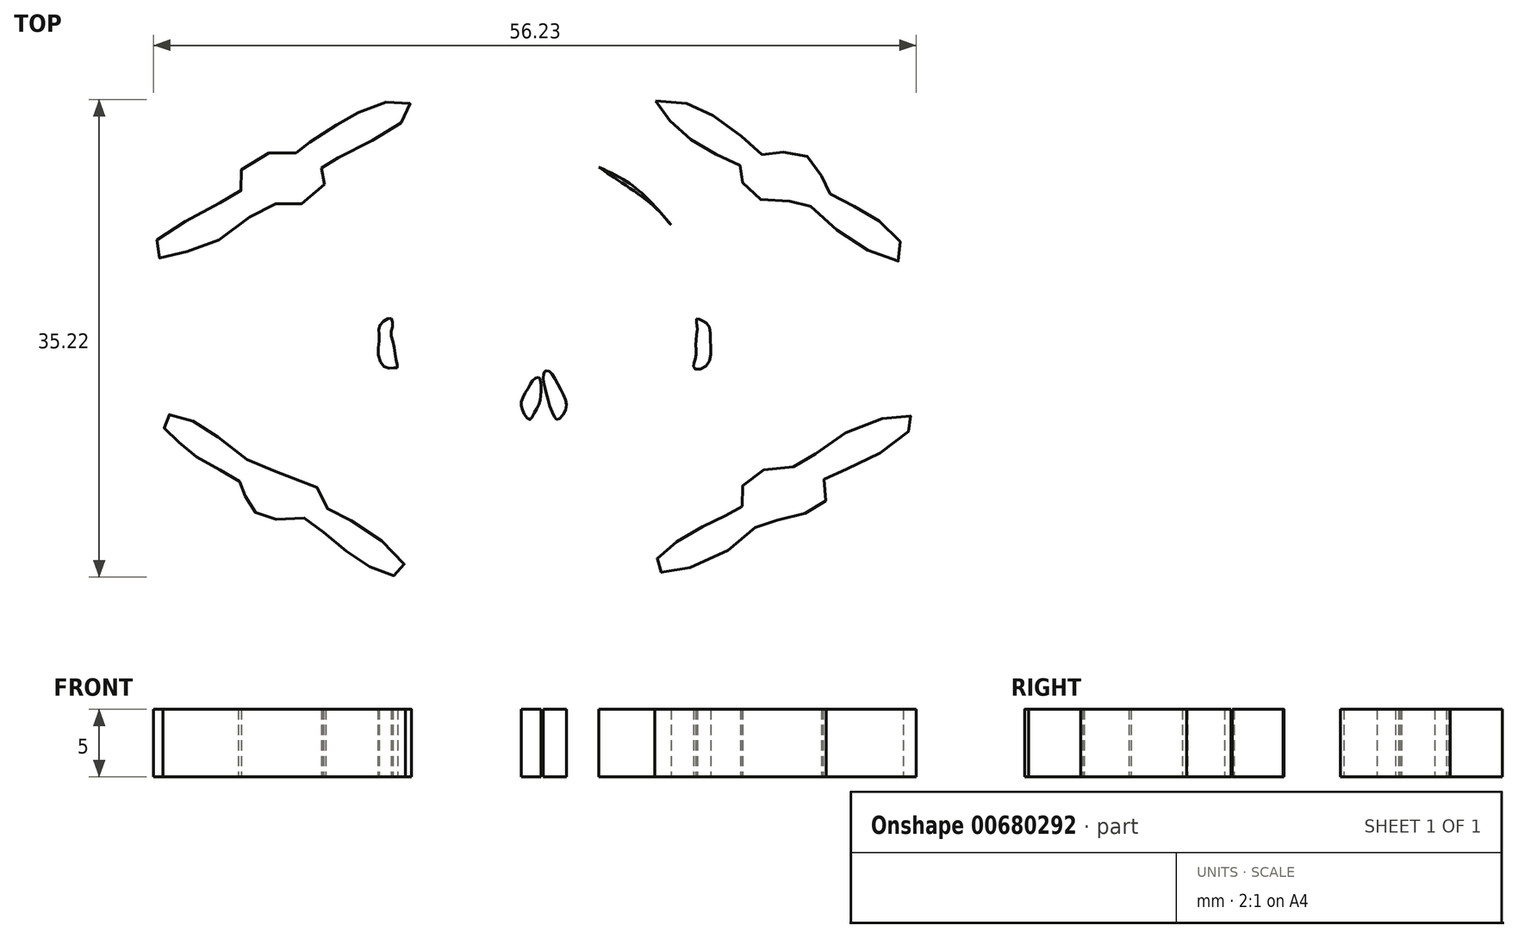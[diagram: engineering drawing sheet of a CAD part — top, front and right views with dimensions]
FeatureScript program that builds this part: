
annotation { "Feature Type Name" : "Feature", "Feature Type Description" : "" }
export const myFeature = defineFeature(function(context is Context, id is Id, definition is map)
    precondition{}
    {
        {
            var Q0;
            Q0=qCreatedBy(makeId("Top.planeOp"),FACE);
            var sketch = newSketch(context, id + "F0", { "sketchPlane" : qUnion([Q0])});
            skFitSpline(sketch, "E0", {"points": [v(10.13, 8.26) * mm, v(10.2, 8.23) * mm, v(10.31, 8.24) * mm, v(10.54, 8.33) * mm, v(11.27, 8.71) * mm, v(11.62, 8.94) * mm, v(11.74, 9.02) * mm, v(11.88, 9.1) * mm, v(12.05, 9.17) * mm, v(12.17, 9.2) * mm, v(12.52, 9.37) * mm, v(13, 9.64) * mm, v(13.46, 9.93) * mm, v(13.75, 10.16) * mm, v(13.84, 10.24) * mm, v(13.9, 10.28) * mm, v(14, 10.28) * mm, v(14.12, 10.26) * mm, v(14.35, 10.23) * mm, v(14.46, 10.12) * mm, v(14.7, 9.87) * mm, v(15.04, 9.58) * mm, v(15.42, 9.37) * mm, v(15.73, 9.26) * mm, v(15.89, 9.21) * mm, v(15.92, 9.01) * mm, v(15.8, 8.92) * mm, v(15.64, 8.77) * mm, v(15.34, 8.59) * mm, v(14.9, 8.31) * mm, v(14.46, 8.04) * mm, v(14.12, 7.8) * mm, v(13.92, 7.64) * mm, v(13.79, 7.51) * mm, v(13.68, 7.48) * mm, v(13.63, 7.45) * mm, v(13.56, 7.42) * mm, v(13.46, 7.34) * mm, v(13.22, 7.14) * mm, v(13.07, 7) * mm, v(12.88, 6.86) * mm, v(12.7, 6.72) * mm, v(12.57, 6.6) * mm, v(12.32, 6.44) * mm, v(12.11, 6.26) * mm, v(11.93, 6.12) * mm, v(11.5, 5.75) * mm, v(11.53, 5.38) * mm, v(11.56, 5.18) * mm, v(11.6, 4.96) * mm, v(11.63, 4.7) * mm, v(11.69, 4.2) * mm, v(11.72, 3.46) * mm, v(11.73, 2.53) * mm, v(11.73, 1.6) * mm, v(11.69, 0.57) * mm, v(11.55, -1.09) * mm, v(11.55, -1.68) * mm, v(11.39, -2.1) * mm, v(11.08, -2.47) * mm, v(10.9, -3.07) * mm, v(10.48, -3.5) * mm, v(10.24, -3.8) * mm, v(10.04, -3.97) * mm, v(10.22, -4.19) * mm, v(10.47, -4.68) * mm, v(11.06, -5.12) * mm, v(11.54, -5.58) * mm, v(12.28, -6.13) * mm, v(13.05, -6.75) * mm, v(13.79, -7.3) * mm, v(14.5, -7.7) * mm, v(15.17, -8.35) * mm, v(15.89, -8.8) * mm, v(15.89, -9.05) * mm, v(15.6, -9.3) * mm, v(15.18, -9.48) * mm, v(14.73, -9.82) * mm, v(14.3, -10.16) * mm, v(13.5, -9.79) * mm, v(12.57, -9.13) * mm, v(11.8, -8.7) * mm, v(10.62, -8.09) * mm, v(10.04, -7.78) * mm, v(9.78, -7.87) * mm, v(9.5, -7.97) * mm, v(9.18, -8.2) * mm, v(8.58, -8.01) * mm, v(8.18, -7.82) * mm, v(7.86, -8) * mm, v(7.23, -8.25) * mm, v(6.68, -8.32) * mm, v(6.3, -8.03) * mm, v(6.17, -7.6) * mm, v(6.4, -6.99) * mm, v(6.6, -6.88) * mm, v(6.02, -6.38) * mm, v(5.65, -6.15) * mm, v(5.28, -5.98) * mm, v(4.82, -5.8) * mm, v(4.78, -6) * mm, v(4.83, -6.32) * mm, v(4.76, -6.63) * mm, v(4.7, -6.86) * mm, v(4.66, -7) * mm, v(4.73, -7.22) * mm, v(4.78, -7.55) * mm, v(4.72, -8.25) * mm, v(4.56, -8.76) * mm, v(4.54, -9.09) * mm, v(4.35, -9.45) * mm, v(4.22, -9.72) * mm, v(4.2, -9.9) * mm, v(3.75, -9.98) * mm, v(3.47, -10) * mm, v(2.92, -10.02) * mm, v(1.78, -10.18) * mm, v(0.94, -10.13) * mm, v(0.27, -10.2) * mm, v(-0.56, -10.11) * mm, v(-1.03, -10.13) * mm, v(-1.83, -9.96) * mm, v(-2.57, -9.93) * mm, v(-3.05, -9.77) * mm, v(-3.28, -9.77) * mm, v(-3.46, -9) * mm, v(-3.75, -8.08) * mm, v(-3.96, -6.87) * mm, v(-3.96, -6.34) * mm, v(-4.25, -6.17) * mm, v(-4.65, -6.04) * mm, v(-5.1, -5.85) * mm, v(-5.39, -5.9) * mm, v(-5.76, -5.98) * mm, v(-5.9, -6.24) * mm, v(-5.86, -6.56) * mm, v(-5.88, -7.03) * mm, v(-5.83, -7.42) * mm, v(-5.87, -7.7) * mm, v(-6.03, -7.86) * mm, v(-6.24, -7.99) * mm, v(-6.65, -8.04) * mm, v(-7.07, -7.88) * mm, v(-7.25, -7.8) * mm, v(-7.7, -7.52) * mm, v(-7.92, -7.27) * mm, v(-8.28, -7.06) * mm, v(-8.54, -7.21) * mm, v(-8.92, -7.31) * mm, v(-9.32, -7.53) * mm, v(-9.97, -7.8) * mm, v(-10.9, -8.41) * mm, v(-11.44, -8.59) * mm, v(-12.43, -9.17) * mm, v(-13.25, -9.75) * mm, v(-14.01, -10.02) * mm, v(-14.3, -10.13) * mm, v(-15.13, -9.67) * mm, v(-15.87, -9.15) * mm, v(-15.93, -8.83) * mm, v(-14.98, -8.3) * mm, v(-14.01, -7.45) * mm, v(-12.66, -6.53) * mm, v(-11.69, -5.72) * mm, v(-10.5, -4.66) * mm, v(-9.37, -3.7) * mm, v(-9, -3.24) * mm, v(-9.47, -2.58) * mm, v(-9.77, -1.84) * mm, v(-9.93, -1.1) * mm, v(-9.92, -0.44) * mm, v(-9.98, 1.9) * mm, v(-10.07, 3.11) * mm, v(-9.95, 4.02) * mm, v(-10.51, 4.66) * mm, v(-11.44, 5.26) * mm, v(-12.28, 6.1) * mm, v(-13.46, 6.98) * mm, v(-15.55, 8.33) * mm, v(-16.03, 8.77) * mm, v(-16.33, 9.04) * mm, v(-15.84, 9.29) * mm, v(-15.1, 9.58) * mm, v(-14.7, 10.05) * mm, v(-14.38, 10.23) * mm, v(-13.96, 9.9) * mm, v(-13.19, 9.6) * mm, v(-12.35, 9.07) * mm, v(-11.41, 8.64) * mm, v(-10.76, 8.11) * mm, v(-9.84, 7.8) * mm, v(-9.25, 7.4) * mm, v(-8.95, 7.46) * mm, v(-8.25, 8.48) * mm, v(-7.51, 9.34) * mm, v(-5.55, 11.08) * mm, v(-4.2, 11.8) * mm, v(-2.84, 12.46) * mm, v(-0.14, 13.03) * mm, v(3.77, 12.96) * mm, v(5.69, 11.91) * mm, v(8.93, 9.56) * mm, v(10.13, 8.26) * mm]});
            skLineSegment(sketch, "E1", {"start": v(10.13, 8.26) * mm, "end": v(10.13, 8.26) * mm});
            skFitSpline(sketch, "E2", {"points": [v(3.77, 12.96) * mm, v(6.66, 11.57) * mm, v(8.5, 10.09) * mm, v(10.13, 8.26) * mm], "startDerivative": vector(8.44, -3.6) * mm, "endDerivative": vector(5.03, -5.92) * mm});
            skFitSpline(sketch, "E3", {"points": [v(-17.54, 13.55) * mm, v(-17.12, 13.84) * mm, v(-16.27, 14.5) * mm, v(-14.26, 15.8) * mm, v(-13.06, 16.48) * mm, v(-11.37, 17.16) * mm, v(-9.48, 17.44) * mm, v(-9.03, 16.93) * mm, v(-9.76, 15.82) * mm, v(-12.03, 14.42) * mm, v(-14.8, 13.04) * mm, v(-15.57, 12.62) * mm, v(-15.63, 12.27) * mm, v(-15.33, 11.63) * mm, v(-16.24, 10.35) * mm, v(-18.03, 9.62) * mm, v(-19.43, 9.81) * mm, v(-21.63, 8.25) * mm, v(-24.27, 6.65) * mm, v(-26.6, 6.05) * mm, v(-27.81, 5.88) * mm, v(-27.94, 6.86) * mm, v(-26.11, 8.27) * mm, v(-23.05, 9.92) * mm, v(-21.6, 10.64) * mm, v(-21.74, 11.4) * mm, v(-21.35, 12.6) * mm, v(-18.98, 13.63) * mm, v(-17.54, 13.55) * mm]});
            skFitSpline(sketch, "E4", {"points": [v(-23.26, -7.4) * mm, v(-24.07, -6.87) * mm, v(-25.7, -5.93) * mm, v(-26.37, -5.8) * mm, v(-27.2, -5.77) * mm, v(-27.33, -6.13) * mm, v(-27.27, -6.68) * mm, v(-26.92, -7.07) * mm, v(-26.36, -7.57) * mm, v(-25.89, -8.06) * mm, v(-25.33, -8.5) * mm, v(-24.1, -9.38) * mm, v(-23.26, -9.76) * mm, v(-22.21, -10.4) * mm, v(-21.77, -10.67) * mm, v(-21.46, -10.72) * mm, v(-21.32, -11.33) * mm, v(-21.28, -11.76) * mm, v(-21.1, -12.4) * mm, v(-20.7, -12.86) * mm, v(-19.81, -13.25) * mm, v(-19.2, -13.42) * mm, v(-18.27, -13.46) * mm, v(-16.88, -13.36) * mm, v(-16, -13.99) * mm, v(-15.41, -14.5) * mm, v(-14.49, -15.34) * mm, v(-13, -16.34) * mm, v(-12.16, -16.92) * mm, v(-11.25, -17.3) * mm, v(-10.18, -17.65) * mm, v(-9.58, -17.63) * mm, v(-9.53, -16.8) * mm, v(-10.65, -15.48) * mm, v(-12.08, -14.43) * mm, v(-13.94, -13.26) * mm, v(-14.78, -12.9) * mm, v(-15.54, -12.35) * mm, v(-15.53, -11.69) * mm, v(-18.2, -9.88) * mm, v(-19.92, -10) * mm, v(-21.68, -8.52) * mm, v(-23.26, -7.4) * mm]});
            skFitSpline(sketch, "E5", {"points": [v(15.38, -12.52) * mm, v(14.94, -12.86) * mm, v(13.62, -13.41) * mm, v(12.15, -14.17) * mm, v(10.18, -15.35) * mm, v(9.1, -16.35) * mm, v(8.97, -17.01) * mm, v(9.68, -17.43) * mm, v(12.25, -16.72) * mm, v(15.7, -14.77) * mm, v(17.03, -13.49) * mm, v(18.85, -13.57) * mm, v(20.76, -12.53) * mm, v(21.55, -12) * mm, v(21.34, -10.7) * mm, v(21.84, -10.2) * mm, v(24.38, -9.21) * mm, v(27.11, -7.43) * mm, v(28.2, -6.1) * mm, v(27.2, -5.76) * mm, v(24.8, -6.35) * mm, v(21.26, -8.13) * mm, v(19.9, -9.42) * mm, v(17.86, -9.63) * mm, v(15.99, -10.33) * mm, v(15.24, -11.53) * mm, v(15.38, -12.52) * mm]});
            skFitSpline(sketch, "E6", {"points": [v(9, 17.4) * mm, v(9.65, 16.33) * mm, v(11.3, 14.77) * mm, v(12.95, 13.7) * mm, v(15.01, 12.77) * mm, v(15.38, 12.36) * mm, v(15.41, 11.33) * mm, v(16.45, 10.23) * mm, v(18.66, 9.96) * mm, v(19.83, 10) * mm, v(21.83, 8.32) * mm, v(24.71, 6.34) * mm, v(27, 5.63) * mm, v(27.18, 6.63) * mm, v(25.83, 8.28) * mm, v(23.95, 9.45) * mm, v(22.2, 10.39) * mm, v(21.25, 11.1) * mm, v(21.13, 12.56) * mm, v(19.55, 13.5) * mm, v(18.26, 13.62) * mm, v(17.03, 13.38) * mm, v(15.9, 14.26) * mm, v(13.38, 16.2) * mm, v(11.56, 17.14) * mm, v(9, 17.4) * mm]});
            skFitSpline(sketch, "E7", {"points": [v(0.94, -1.9) * mm, v(0.39, -2.03) * mm, v(-0.75, -2.48) * mm, v(-3.17, -4.09) * mm, v(-5.93, -4.65) * mm, v(-7.8, -4.2) * mm, v(-8.04, -4.17) * mm, v(-8.25, -4.75) * mm, v(-8.38, -5.76) * mm, v(-7.1, -7.18) * mm, v(-6.32, -7.45) * mm, v(-6.37, -6.6) * mm, v(-6.39, -5.87) * mm, v(-5.58, -5.3) * mm, v(-3.96, -5.64) * mm, v(-3.38, -6.89) * mm, v(-3.17, -8.13) * mm, v(-2.75, -9.33) * mm, v(-1.4, -9.67) * mm, v(-1.34, -9.13) * mm, v(-1.83, -8.1) * mm, v(-1.2, -7.73) * mm, v(-0.68, -7.97) * mm, v(-0.6, -8.72) * mm, v(-0.6, -9.72) * mm, v(-0.23, -9.77) * mm, v(0.22, -9.7) * mm, v(0.3, -8.97) * mm, v(0.6, -8.2) * mm, v(1.06, -8.44) * mm, v(1.04, -9.24) * mm, v(1.16, -9.8) * mm, v(2.1, -9.68) * mm, v(2.35, -8.41) * mm, v(2.82, -8.47) * mm, v(2.99, -9.5) * mm, v(3.43, -9.59) * mm, v(3.87, -9.37) * mm, v(4.17, -8.38) * mm, v(4.24, -7.66) * mm, v(4.02, -7.12) * mm, v(4.34, -6.58) * mm, v(4.17, -5.64) * mm, v(4.98, -5.27) * mm, v(5.95, -5.66) * mm, v(6.96, -6.34) * mm, v(7.26, -7.02) * mm, v(6.86, -7.52) * mm, v(6.56, -7.64) * mm, v(6.74, -7.74) * mm, v(7.53, -7.61) * mm, v(8.1, -7.37) * mm, v(8.76, -7.5) * mm, v(9.23, -7.44) * mm, v(9.92, -6.34) * mm, v(9.85, -5) * mm, v(9.6, -4.33) * mm, v(9, -4.46) * mm, v(7.35, -4.6) * mm, v(5.53, -4.33) * mm, v(3.9, -3.44) * mm, v(2.5, -2.5) * mm, v(1.75, -2.04) * mm, v(0.94, -1.9) * mm]});
            skFitSpline(sketch, "E8", {"points": [v(0.35, -2.97) * mm, v(0, -3.17) * mm, v(-0.33, -3.65) * mm, v(-0.81, -4.48) * mm, v(-0.91, -5.08) * mm, v(-0.65, -5.77) * mm, v(-0.28, -6.1) * mm, v(0, -5.7) * mm, v(0.39, -4.97) * mm, v(0.52, -4.3) * mm, v(0.53, -3.54) * mm, v(0.45, -3.05) * mm, v(0.35, -2.97) * mm]});
            skFitSpline(sketch, "E9", {"points": [v(0.94, -2.5) * mm, v(1.2, -2.57) * mm, v(1.76, -3.46) * mm, v(2.33, -4.57) * mm, v(2.34, -5.44) * mm, v(1.8, -6.09) * mm, v(1.58, -5.97) * mm, v(1.09, -4.79) * mm, v(0.78, -3.54) * mm, v(0.71, -2.86) * mm, v(0.8, -2.57) * mm, v(0.94, -2.5) * mm]});
            skFitSpline(sketch, "E10", {"points": [v(-9.42, 2.63) * mm, v(-9.32, 4.1) * mm, v(-8.82, 6.36) * mm, v(-8.05, 7.8) * mm, v(-5.32, 10.63) * mm, v(-3.69, 11.56) * mm, v(-2.05, 12.03) * mm, v(0.26, 12.53) * mm, v(1.75, 12.56) * mm, v(3.73, 12.32) * mm, v(6.97, 10.77) * mm, v(8.52, 9.13) * mm, v(10.4, 6.84) * mm, v(11.03, 4.45) * mm, v(11.3, 2.6) * mm, v(10.88, 2.65) * mm, v(8.08, 3.1) * mm, v(7.85, 4.24) * mm, v(7.85, 6.26) * mm, v(8.29, 6.28) * mm, v(9, 6.28) * mm, v(9.24, 6.34) * mm, v(9.4, 6.46) * mm, v(9.22, 6.75) * mm, v(8.6, 7.31) * mm, v(7.49, 7.65) * mm, v(6.62, 7.5) * mm, v(5.7, 6.92) * mm, v(5.3, 6.52) * mm, v(5.33, 6.36) * mm, v(5.82, 6.33) * mm, v(6.57, 6.31) * mm, v(6.96, 6.34) * mm, v(7, 6.2) * mm, v(6.98, 5.42) * mm, v(6.96, 3.28) * mm, v(6.92, 3.17) * mm, v(6.54, 3.25) * mm, v(5.35, 3.38) * mm, v(1.75, 3.42) * mm, v(-2.66, 3.37) * mm, v(-5.47, 3) * mm, v(-5.57, 3.13) * mm, v(-5.55, 3.3) * mm, v(-5.52, 6.29) * mm, v(-5.37, 6.36) * mm, v(-5.05, 6.36) * mm, v(-4.66, 6.31) * mm, v(-3.96, 6.34) * mm, v(-4.41, 6.98) * mm, v(-5.4, 7.62) * mm, v(-6.5, 7.52) * mm, v(-7.37, 7.13) * mm, v(-8.17, 6.54) * mm, v(-7.94, 6.33) * mm, v(-7.03, 6.33) * mm, v(-6.49, 6.3) * mm, v(-6.4, 6.17) * mm, v(-6.43, 5.78) * mm, v(-6.44, 3.5) * mm, v(-6.6, 3.05) * mm, v(-7.85, 2.83) * mm, v(-9.42, 2.63) * mm]});
            skFitSpline(sketch, "E11", {"points": [v(-10.51, 1.37) * mm, v(-10.4, 0.83) * mm, v(-10.51, 0.27) * mm, v(-10.31, -0.65) * mm, v(-10.18, -1.64) * mm, v(-10.05, -2.25) * mm, v(-10.23, -2.28) * mm, v(-10.9, -2.25) * mm, v(-11.46, -1.36) * mm, v(-11.39, 0) * mm, v(-11.39, 0.76) * mm, v(-10.9, 1.25) * mm, v(-10.51, 1.37) * mm]});
            skFitSpline(sketch, "E12", {"points": [v(12.01, 1.33) * mm, v(12.05, 0.75) * mm, v(11.97, -0.1) * mm, v(11.95, -0.7) * mm, v(11.99, -1.29) * mm, v(11.85, -1.77) * mm, v(11.78, -2.11) * mm, v(11.86, -2.36) * mm, v(12.57, -2.26) * mm, v(13.04, -1.41) * mm, v(13.02, -0.16) * mm, v(12.91, 0.8) * mm, v(12.5, 1.17) * mm, v(12.17, 1.32) * mm, v(12.01, 1.33) * mm]});
            skSolve(sketch);
        }
        {
            var Q0;
            Q0=makeQuery(id+"F0.imprint","IMPRINT",FACE,{"disambiguationData":[TD([[makeQuery(id+"F0.imprint","IMPRINT",EDGE,{"derivedFrom":sQuery(id+"F0.wireOp",EDGE,"E4")}),1.0]])]});
            var Q1;
            Q1=makeQuery(id+"F0.imprint","IMPRINT",FACE,{"disambiguationData":[TD([[makeQuery(id+"F0.imprint","IMPRINT",EDGE,{"derivedFrom":sQuery(id+"F0.wireOp",EDGE,"E3")}),-1.0]])]});
            var Q2;
            Q2=makeQuery(id+"F0.imprint","IMPRINT",FACE,{"disambiguationData":[TD([[makeQuery(id+"F0.imprint","IMPRINT",EDGE,{"derivedFrom":sQuery(id+"F0.wireOp",EDGE,"E6")}),1.0]])]});
            var Q3;
            {var subQ0=sQuery(id+"F0.wireOp",EDGE,"E2");Q3=makeQuery(id+"F0.imprint","IMPRINT",FACE,{"disambiguationData":[TD([[makeQuery(id+"F0.imprint","IMPRINT",EDGE,{"derivedFrom":subQ0}),-1.0]])]});}
            var Q4;
            Q4=makeQuery(id+"F0.imprint","IMPRINT",FACE,{"disambiguationData":[TD([[makeQuery(id+"F0.imprint","IMPRINT",EDGE,{"derivedFrom":sQuery(id+"F0.wireOp",EDGE,"E11")}),-1.0]])]});
            var Q5;
            Q5=makeQuery(id+"F0.imprint","IMPRINT",FACE,{"disambiguationData":[TD([[makeQuery(id+"F0.imprint","IMPRINT",EDGE,{"derivedFrom":sQuery(id+"F0.wireOp",EDGE,"E12")}),1.0]])]});
            var Q6;
            Q6=makeQuery(id+"F0.imprint","IMPRINT",FACE,{"disambiguationData":[TD([[makeQuery(id+"F0.imprint","IMPRINT",EDGE,{"derivedFrom":sQuery(id+"F0.wireOp",EDGE,"E5")}),1.0]])]});
            var Q7;
            Q7=makeQuery(id+"F0.imprint","IMPRINT",FACE,{"disambiguationData":[TD([[makeQuery(id+"F0.imprint","IMPRINT",EDGE,{"derivedFrom":sQuery(id+"F0.wireOp",EDGE,"E9")}),-1.0]])]});
            var Q8;
            Q8=makeQuery(id+"F0.imprint","IMPRINT",FACE,{"disambiguationData":[TD([[makeQuery(id+"F0.imprint","IMPRINT",EDGE,{"derivedFrom":sQuery(id+"F0.wireOp",EDGE,"E8")}),1.0]])]});
            extrude(context, id + "F1", {"entities" : qUnion([Q0, Q1, Q2, Q3, Q4, Q5, Q6, Q7, Q8]), "depth" : 5 * mm, "offsetDistance" : 25 * mm});
        }
    });
